# Revit family: QF_BPRO_BT 400_566316
name_source: partatom
category: Sonderausstattung
revit_build: Autodesk Revit 2018 (Build: 20190510_1515(x64)
units: mm (PartAtom-declared; Revit-internal decimal feet)

## family parameters
Arbeitsebenenbasiert = Nein
Beim Laden mit Abzugskörper schneiden = Nein
Bemaßung runder Anschluss = Durchmesser verwenden
Gemeinsam genutzt = Nein
Immer vertikal = Ja
Raumberechnungspunkt = Ja
Teiletyp = Normal

## types (1)
- BT 400
    Artikel Nummer = 566316
    Beschreibung = Besteck- und Tablettwagen inkl. 5 Besteckbehälter
    Beschreibung durch Hersteller analog Leistungsverzeichniskurztext = Abmessungen

Länge:			  900 mm
Breite:		  600 mm  
Höhe:		  1270 mm


Ausführung

Der Besteck- und Tablettwagen ist mit einem pultförmigen Besteckaufsatz inkl. 5 Besteckbehälter der Größe GN 1/4-150 aus CNS versehen. Beide Stirnseiten sind durch Kunststoff- Formschlussteile geschlossen. Das Fahrgestell ist aus stabilem 25 x 25 mm Vierkantrohr gebogen, dazwischen befindet sich ein Bord für die Tablettaufnahme. Das Bord ist eingeschweißt und hinten 50 mm aufgekantet (Durchschubsicherung).
Aus hygienischen Gründen sind alle Besteckbehälter mit transparenter, halbseitig klappbarer Plexiglas¬abdeckung ausgeführt. Der Behälterboden ist für ein gutes Greifen der Besteckteile entsprechend abgeschrägt. Speziell für Kuchengabeln und Kaffeelöffel ist der letzte Besteckbehälter mit  senkrechter Unterteilung. Im rechten Bereich direkt unter dem Aufsatz ist ein Serviettenspender für die Größe 125 x 90 mm aus CNS montiert, dieser ist von vorne beschickbar.

Der Besteck- und Tablettwagen ist fahrbar mittels stahlverzinkten Rollen (4 Lenkrollen, davon 2 mit Feststeller, Rollendurchmesser 125 mm). An allen vier Ecken befinden sich runde Wandabweiser.


Zubehör

•	Zusätzliches Bord

Technische Daten

Werkstoff:   CNS 18/10
Gewicht:	   25,05 kg
Kapazität:   500 Besteckteile; 120 Tabletts (Gastro-	oder Euronorm)

Besonderheit:   Servietten-Spender unter dem Aufsatz

Fabrikat
Hersteller:   B.PRO
Modell:	    BT 400
Best.Nr.	    566316
    Beschreibung durch Hersteller analog Leistungsverzeichnislangtext = Abmessungen

Länge:			  900 mm
Breite:		  600 mm  
Höhe:		  1270 mm


Ausführung

Der Besteck- und Tablettwagen ist mit einem pultförmigen Besteckaufsatz inkl. 5 Besteckbehälter der Größe GN 1/4-150 aus CNS versehen. Beide Stirnseiten sind durch Kunststoff- Formschlussteile geschlossen. Das Fahrgestell ist aus stabilem 25 x 25 mm Vierkantrohr gebogen, dazwischen befindet sich ein Bord für die Tablettaufnahme. Das Bord ist eingeschweißt und hinten 50 mm aufgekantet (Durchschubsicherung).
Aus hygienischen Gründen sind alle Besteckbehälter mit transparenter, halbseitig klappbarer Plexiglas¬abdeckung ausgeführt. Der Behälterboden ist für ein gutes Greifen der Besteckteile entsprechend abgeschrägt. Speziell für Kuchengabeln und Kaffeelöffel ist der letzte Besteckbehälter mit  senkrechter Unterteilung. Im rechten Bereich direkt unter dem Aufsatz ist ein Serviettenspender für die Größe 125 x 90 mm aus CNS montiert, dieser ist von vorne beschickbar.

Der Besteck- und Tablettwagen ist fahrbar mittels stahlverzinkten Rollen (4 Lenkrollen, davon 2 mit Feststeller, Rollendurchmesser 125 mm). An allen vier Ecken befinden sich runde Wandabweiser.


Zubehör

•	Zusätzliches Bord

Technische Daten

Werkstoff:   CNS 18/10
Gewicht:	   25,05 kg
Kapazität:   500 Besteckteile; 120 Tabletts (Gastro-	oder Euronorm)

Besonderheit:   Servietten-Spender unter dem Aufsatz

Fabrikat
Hersteller:   B.PRO
Modell:	    BT 400
Best.Nr.	    566316
    CE Kennzeichnung = Ja
    Gerätegewicht Netto = 24.00 kg
    Großküchengerätezuordnung = Ja
    Hersteller = B.PRO GmbH
    Höhe = 1259 mm
    Internetadresse Gerätehersteller = https://www.bpro-solutions.com
    Internetadresse für Ersatzteilliste = https://www.bpro-solutions.com
    Kosten = 1387 $
    Länge Gerätebreite = 901 mm  [stored 2.95604 ft]
    Material = <Nach Kategorie>
    Modell = BT 400
    Sockelhöhe = 173 mm
    Tiefe = 601 mm
    Typenkommentare = Besteck- und Tablettwagen inkl. 5 Besteckbehälter
    URL = https://www.bpro-solutions.com
    Zubehör = Ja

note: [stored X ft] marks values corroborated as IEEE doubles in the binary element streams (Revit-internal decimal feet)
